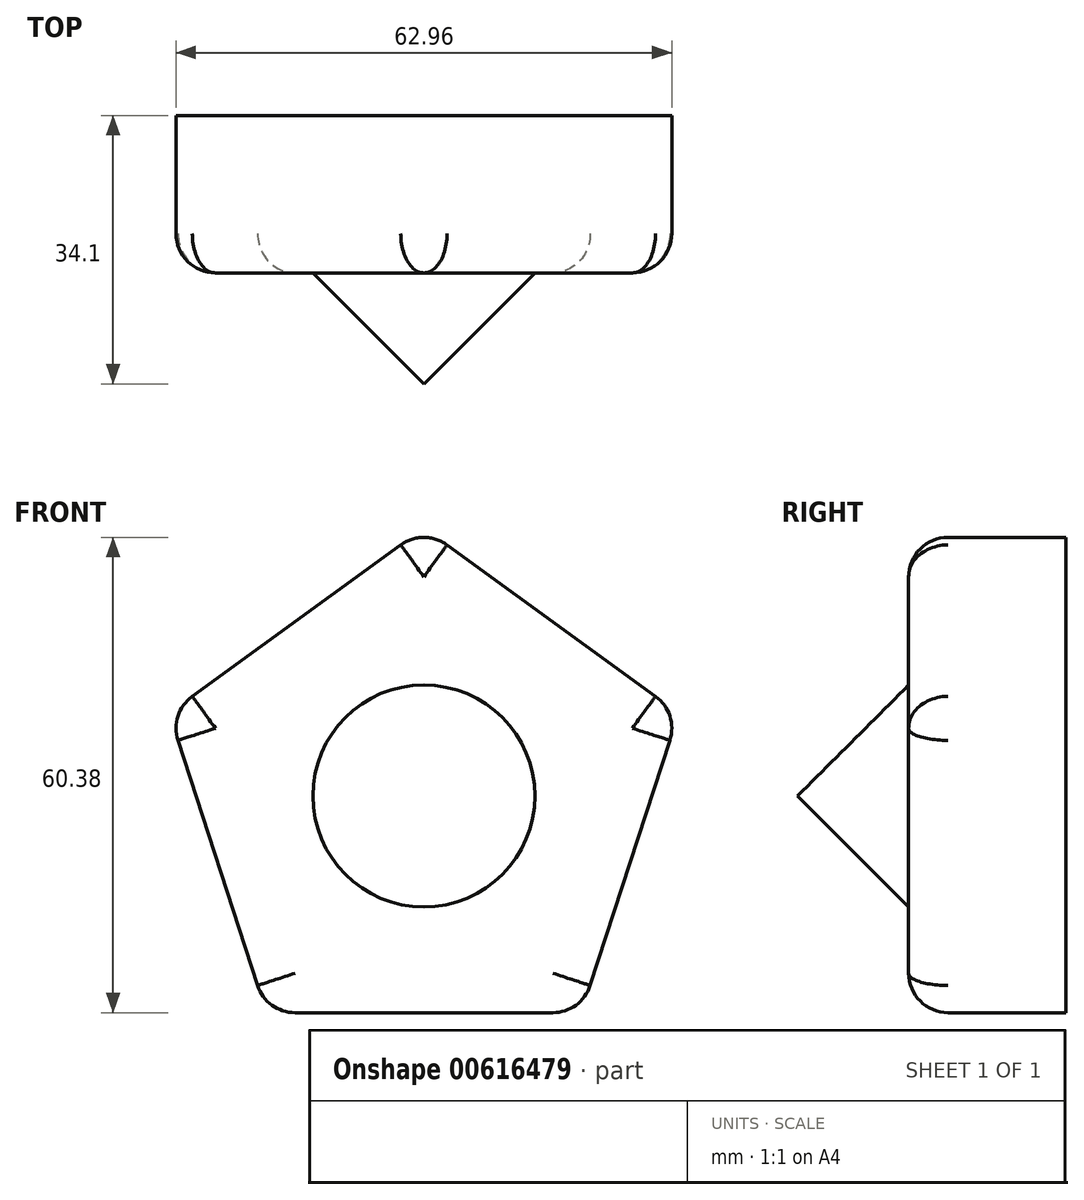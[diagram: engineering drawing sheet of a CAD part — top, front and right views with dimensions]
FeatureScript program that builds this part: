
annotation { "Feature Type Name" : "Feature", "Feature Type Description" : "" }
export const myFeature = defineFeature(function(context is Context, id is Id, definition is map)
    precondition{}
    {
        {
            var Q0;
            Q0=qCreatedBy(makeId("Front.planeOp"),FACE);
            var sketch = newSketch(context, id + "F0", { "sketchPlane" : qUnion([Q0])});
            skCircle(sketch, "E0.cCircle", {"center": v(0, 0) * mm, "radius": 27.53 * mm, "construction": true});
            skLineSegment(sketch, "E0.0", {"start": v(20, -27.53) * mm, "end": v(-20, -27.53) * mm});
            skLineSegment(sketch, "E0.1", {"start": v(-20, -27.53) * mm, "end": v(-32.36, 10.51) * mm});
            skLineSegment(sketch, "E0.2", {"start": v(-32.36, 10.51) * mm, "end": v(0, 34.03) * mm});
            skLineSegment(sketch, "E0.3", {"start": v(0, 34.03) * mm, "end": v(32.36, 10.51) * mm});
            skLineSegment(sketch, "E0.4", {"start": v(32.36, 10.51) * mm, "end": v(20, -27.53) * mm});
            skPoint(sketch, "E0.0.midPoint", {"position": v(0, -27.53) * mm});
            skCircle(sketch, "E1", {"center": v(0, 0) * mm, "radius": 15 * mm});
            skSolve(sketch);
        }
        {
            var Q0;
            Q0=makeQuery(id+"F0.imprint","IMPRINT",FACE,{"disambiguationData":[TD([[makeQuery(id+"F0.imprint","IMPRINT",EDGE,{"derivedFrom":sQuery(id+"F0.wireOp",EDGE,"E0.0")}),-1.0]])]});
            extrude(context, id + "F1", {"entities" : qUnion([Q0]), "depth" : 20 * mm, "offsetDistance" : 25 * mm});
        }
        {
            var Q0;
            Q0=makeQuery(id+"F1.opExtrude","CAP_EDGE",EDGE,{"disambiguationData":[OSD([sQuery(id+"F0.wireOp",EDGE,"E0.1")])],"isStart":false});
            var Q1;
            Q1=makeQuery(id+"F1.opExtrude","CAP_EDGE",EDGE,{"disambiguationData":[OSD([sQuery(id+"F0.wireOp",EDGE,"E0.0")])],"isStart":false});
            var Q2;
            Q2=makeQuery(id+"F1.opExtrude","CAP_EDGE",EDGE,{"disambiguationData":[OSD([sQuery(id+"F0.wireOp",EDGE,"E0.4")])],"isStart":false});
            var Q3;
            Q3=makeQuery(id+"F1.opExtrude","CAP_EDGE",EDGE,{"disambiguationData":[OSD([sQuery(id+"F0.wireOp",EDGE,"E0.3")])],"isStart":false});
            var Q4;
            Q4=makeQuery(id+"F1.opExtrude","CAP_EDGE",EDGE,{"disambiguationData":[OSD([sQuery(id+"F0.wireOp",EDGE,"E0.2")])],"isStart":false});
            fillet(context, id + "F2", {"entities" : qUnion([Q0, Q1, Q2, Q3, Q4]), "radius" : 5 * mm, "tangentPropagation" : true, "allowEdgeOverflow" : false});
        }
        {
            var Q0;
            Q0=makeQuery(id+"F1.opExtrude","SWEPT_EDGE",EDGE,{"disambiguationData":[OSD([sQuery(id+"F0.wireOp",EDGE,"E0.0"),sQuery(id+"F0.wireOp",EDGE,"E0.4")])]});
            var Q1;
            Q1=makeQuery(id+"F1.opExtrude","SWEPT_EDGE",EDGE,{"disambiguationData":[OSD([sQuery(id+"F0.wireOp",EDGE,"E0.3"),sQuery(id+"F0.wireOp",EDGE,"E0.4")])]});
            var Q2;
            Q2=makeQuery(id+"F1.opExtrude","SWEPT_EDGE",EDGE,{"disambiguationData":[OSD([sQuery(id+"F0.wireOp",EDGE,"E0.2"),sQuery(id+"F0.wireOp",EDGE,"E0.3")])]});
            var Q3;
            Q3=makeQuery(id+"F1.opExtrude","SWEPT_EDGE",EDGE,{"disambiguationData":[OSD([sQuery(id+"F0.wireOp",EDGE,"E0.1"),sQuery(id+"F0.wireOp",EDGE,"E0.2")])]});
            var Q4;
            Q4=makeQuery(id+"F1.opExtrude","SWEPT_EDGE",EDGE,{"disambiguationData":[OSD([sQuery(id+"F0.wireOp",EDGE,"E0.0"),sQuery(id+"F0.wireOp",EDGE,"E0.1")])]});
            fillet(context, id + "F3", {"entities" : qUnion([Q0, Q1, Q2, Q3, Q4]), "radius" : 5 * mm, "tangentPropagation" : true, "allowEdgeOverflow" : false});
        }
        {
            var Q0;
            Q0=makeQuery(id+"F0.imprint","IMPRINT",FACE,{"disambiguationData":[TD([[makeQuery(id+"F0.imprint","IMPRINT",EDGE,{"derivedFrom":sQuery(id+"F0.wireOp",EDGE,"E1")}),1.0]])]});
            extrude(context, id + "F4", {"entities" : qUnion([Q0]), "operationType" : NewBodyOperationType.ADD, "depth" : 34.1 * mm, "offsetDistance" : 25 * mm});
        }
        {
            var Q0;
            Q0=makeQuery(id+"F4.opExtrude","CAP_EDGE",EDGE,{"disambiguationData":[OSD([sQuery(id+"F0.wireOp",EDGE,"E1")])],"isStart":false});
            chamfer(context, id + "F5", {"entities" : qUnion([Q0]), "width" : 15 * mm, "tangentPropagation" : true});
        }
    });
